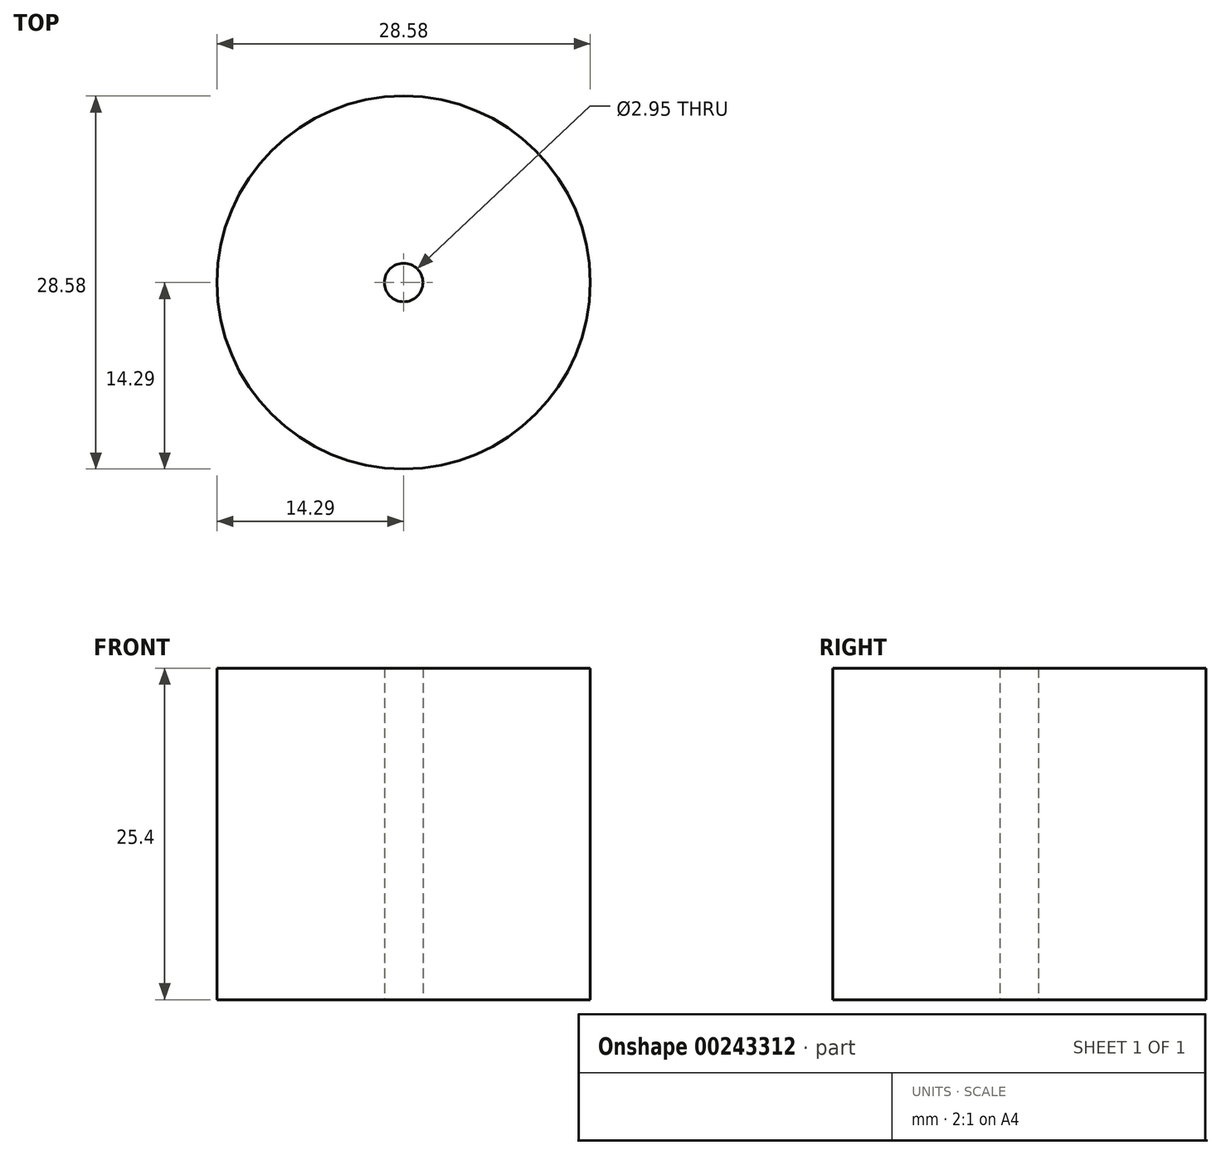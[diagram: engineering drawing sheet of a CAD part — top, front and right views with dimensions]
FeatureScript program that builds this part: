
annotation { "Feature Type Name" : "Feature", "Feature Type Description" : "" }
export const myFeature = defineFeature(function(context is Context, id is Id, definition is map)
    precondition{}
    {
        {
            var Q0;
            Q0=qCreatedBy(makeId("Top.planeOp"),FACE);
            var sketch = newSketch(context, id + "F0", { "sketchPlane" : qUnion([Q0])});
            skCircle(sketch, "E0", {"center": v(0, 0) * mm, "radius": 14.29 * mm});
            skCircle(sketch, "E1", {"center": v(0, 0) * mm, "radius": 1.47 * mm});
            skSolve(sketch);
        }
        {
            var Q0;
            Q0 = qSketchRegion(id + "F0", true);
            extrude(context, id + "F1", {"entities" : qUnion([Q0]), "depth" : 25.4 * mm});
        }
    });
